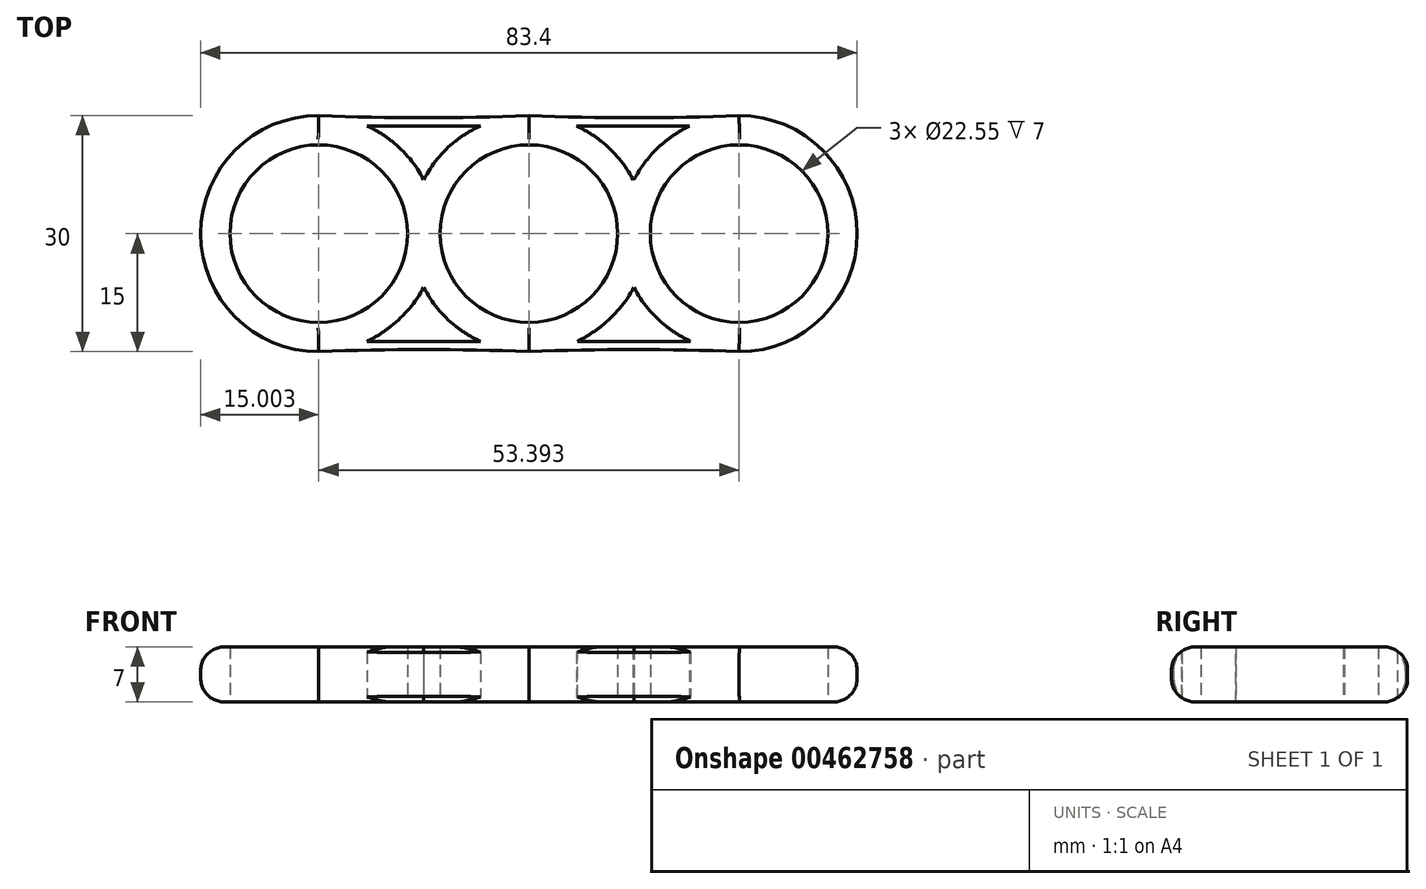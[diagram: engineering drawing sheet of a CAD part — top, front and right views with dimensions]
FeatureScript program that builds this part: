
annotation { "Feature Type Name" : "Feature", "Feature Type Description" : "" }
export const myFeature = defineFeature(function(context is Context, id is Id, definition is map)
    precondition{}
    {
        {
            var Q0;
            Q0=qCreatedBy(makeId("Top.planeOp"),FACE);
            var sketch = newSketch(context, id + "F0", { "sketchPlane" : qUnion([Q0])});
            skCircle(sketch, "E0", {"center": v(0, 0) * mm, "radius": 11.28 * mm});
            skCircle(sketch, "E1", {"center": v(0, 0) * mm, "radius": 15 * mm});
            skCircle(sketch, "E2", {"center": v(0, 0) * mm, "radius": 26.7 * mm});
            skCircle(sketch, "E3", {"center": v(26.7, 0) * mm, "radius": 11.28 * mm});
            skCircle(sketch, "E4", {"center": v(-26.7, 0) * mm, "radius": 11.28 * mm});
            skCircle(sketch, "E5", {"center": v(-26.7, 0) * mm, "radius": 15 * mm});
            skCircle(sketch, "E6", {"center": v(26.7, 0) * mm, "radius": 15 * mm});
            skArc(sketch, "E7", {"start": v(-26.7, 15) * mm, "mid": v(-13.35, 14.72) * mm, "end": v(0, 15) * mm});
            skArc(sketch, "E8", {"start": v(0, 15) * mm, "mid": v(13.35, 14.72) * mm, "end": v(26.7, 15) * mm});
            skArc(sketch, "E9", {"start": v(0, -15) * mm, "mid": v(-13.35, -14.72) * mm, "end": v(-26.7, -15) * mm});
            skArc(sketch, "E10", {"start": v(26.7, -15) * mm, "mid": v(13.35, -14.72) * mm, "end": v(0, -15) * mm});
            skArc(sketch, "E11", {"start": v(-13.35, 6.84) * mm, "mid": v(-16.38, 10.85) * mm, "end": v(-20.54, 13.68) * mm});
            skArc(sketch, "E12", {"start": v(-6.15, 13.68) * mm, "mid": v(-10.28, 10.81) * mm, "end": v(-13.35, 6.84) * mm});
            skLineSegment(sketch, "E13", {"start": v(-20.54, 13.68) * mm, "end": v(-6.15, 13.68) * mm});
            skArc(sketch, "E14", {"start": v(-13.35, -6.84) * mm, "mid": v(-10.31, -10.85) * mm, "end": v(-6.15, -13.68) * mm});
            skArc(sketch, "E15", {"start": v(-20.54, -13.68) * mm, "mid": v(-16.42, -10.81) * mm, "end": v(-13.35, -6.84) * mm});
            skLineSegment(sketch, "E16", {"start": v(-6.15, -13.68) * mm, "end": v(-20.54, -13.68) * mm});
            skArc(sketch, "E17", {"start": v(13.35, -6.84) * mm, "mid": v(16.38, -10.85) * mm, "end": v(20.54, -13.68) * mm});
            skArc(sketch, "E18", {"start": v(6.15, -13.68) * mm, "mid": v(10.28, -10.81) * mm, "end": v(13.35, -6.84) * mm});
            skLineSegment(sketch, "E19", {"start": v(20.54, -13.68) * mm, "end": v(6.15, -13.68) * mm});
            skArc(sketch, "E20", {"start": v(13.23, 6.84) * mm, "mid": v(10.2, 10.85) * mm, "end": v(6.03, 13.68) * mm});
            skArc(sketch, "E21", {"start": v(20.42, 13.68) * mm, "mid": v(16.3, 10.81) * mm, "end": v(13.23, 6.84) * mm});
            skLineSegment(sketch, "E22", {"start": v(6.03, 13.68) * mm, "end": v(20.42, 13.68) * mm});
            skSolve(sketch);
        }
        {
            var Q0;
            {var subQ1=sQuery(id+"F0.wireOp",EDGE,"E5");var subQ3=sQuery(id+"F0.wireOp",EDGE,"E2");var subQ4=makeQuery(id+"F0.imprint","INTERSECT",VERTEX,{"disambiguationData":[OD(0.0)],"derivedFrom":[subQ3,subQ1]});Q0=makeQuery(id+"F0.imprint","IMPRINT",FACE,{"disambiguationData":[TD([[makeQuery(id+"F0.imprint","IMPRINT",EDGE,{"disambiguationData":[TD([[subQ4,-1.0]])],"derivedFrom":subQ3}),-1.0]])]});}
            var Q1;
            {var subQ0=sQuery(id+"F0.wireOp",EDGE,"E5");var subQ1=sQuery(id+"F0.wireOp",EDGE,"E1");var subQ2=makeQuery(id+"F0.imprint","INTERSECT",VERTEX,{"disambiguationData":[OD(0.0)],"derivedFrom":[subQ1,subQ0]});Q1=makeQuery(id+"F0.imprint","IMPRINT",FACE,{"disambiguationData":[TD([[makeQuery(id+"F0.imprint","IMPRINT",EDGE,{"disambiguationData":[TD([[subQ2,-1.0]])],"derivedFrom":subQ1}),1.0]])]});}
            var Q2;
            Q2=makeQuery(id+"F0.imprint","IMPRINT",FACE,{"disambiguationData":[TD([[makeQuery(id+"F0.imprint","IMPRINT",EDGE,{"derivedFrom":sQuery(id+"F0.wireOp",EDGE,"E0")}),-1.0]])]});
            var Q3;
            {var subQ4=sQuery(id+"F0.wireOp",EDGE,"E6");var subQ6=sQuery(id+"F0.wireOp",EDGE,"E1");var subQ7=makeQuery(id+"F0.imprint","INTERSECT",VERTEX,{"disambiguationData":[OD(0.0)],"derivedFrom":[subQ6,subQ4]});Q3=makeQuery(id+"F0.imprint","IMPRINT",FACE,{"disambiguationData":[TD([[makeQuery(id+"F0.imprint","IMPRINT",EDGE,{"disambiguationData":[TD([[subQ7,1.0]])],"derivedFrom":subQ6}),-1.0]])]});}
            var Q4;
            {var subQ0=sQuery(id+"F0.wireOp",EDGE,"E10");var subQ1=sQuery(id+"F0.wireOp",EDGE,"E1");var subQ2=makeQuery(id+"F0.imprint","INTERSECT",VERTEX,{"derivedFrom":[subQ1,subQ0]});Q4=makeQuery(id+"F0.imprint","IMPRINT",FACE,{"disambiguationData":[TD([[makeQuery(id+"F0.imprint","IMPRINT",EDGE,{"disambiguationData":[TD([[subQ2,-1.0]])],"derivedFrom":subQ1}),-1.0]])]});}
            var Q5;
            {var subQ0=sQuery(id+"F0.wireOp",EDGE,"E6");var subQ1=sQuery(id+"F0.wireOp",EDGE,"E1");var subQ2=makeQuery(id+"F0.imprint","INTERSECT",VERTEX,{"disambiguationData":[OD(0.0)],"derivedFrom":[subQ1,subQ0]});Q5=makeQuery(id+"F0.imprint","IMPRINT",FACE,{"disambiguationData":[TD([[makeQuery(id+"F0.imprint","IMPRINT",EDGE,{"disambiguationData":[TD([[subQ2,1.0]])],"derivedFrom":subQ1}),1.0]])]});}
            var Q6;
            {var subQ0=sQuery(id+"F0.wireOp",EDGE,"E7");var subQ1=sQuery(id+"F0.wireOp",EDGE,"E1");var subQ2=makeQuery(id+"F0.imprint","INTERSECT",VERTEX,{"derivedFrom":[subQ1,subQ0]});Q6=makeQuery(id+"F0.imprint","IMPRINT",FACE,{"disambiguationData":[TD([[makeQuery(id+"F0.imprint","IMPRINT",EDGE,{"disambiguationData":[TD([[subQ2,-1.0]])],"derivedFrom":subQ1}),-1.0]])]});}
            var Q7;
            {var subQ0=sQuery(id+"F0.wireOp",EDGE,"E8");var subQ1=sQuery(id+"F0.wireOp",EDGE,"E1");var subQ2=makeQuery(id+"F0.imprint","INTERSECT",VERTEX,{"derivedFrom":[subQ1,subQ0]});Q7=makeQuery(id+"F0.imprint","IMPRINT",FACE,{"disambiguationData":[TD([[makeQuery(id+"F0.imprint","IMPRINT",EDGE,{"disambiguationData":[TD([[subQ2,1.0]])],"derivedFrom":subQ1}),-1.0]])]});}
            var Q8;
            {var subQ1=sQuery(id+"F0.wireOp",EDGE,"E2");var subQ5=sQuery(id+"F0.wireOp",EDGE,"E6");var subQ7=makeQuery(id+"F0.imprint","INTERSECT",VERTEX,{"disambiguationData":[OD(0.0)],"derivedFrom":[subQ1,subQ5]});Q8=makeQuery(id+"F0.imprint","IMPRINT",FACE,{"disambiguationData":[TD([[makeQuery(id+"F0.imprint","IMPRINT",EDGE,{"disambiguationData":[TD([[subQ7,1.0]])],"derivedFrom":subQ1}),-1.0]])]});}
            var Q9;
            {var subQ0=sQuery(id+"F0.wireOp",EDGE,"E7");var subQ1=sQuery(id+"F0.wireOp",EDGE,"E2");var subQ2=makeQuery(id+"F0.imprint","INTERSECT",VERTEX,{"derivedFrom":[subQ1,subQ0]});Q9=makeQuery(id+"F0.imprint","IMPRINT",FACE,{"disambiguationData":[TD([[makeQuery(id+"F0.imprint","IMPRINT",EDGE,{"disambiguationData":[TD([[subQ2,-1.0]])],"derivedFrom":subQ1}),-1.0]])]});}
            var Q10;
            {var subQ0=sQuery(id+"F0.wireOp",EDGE,"E9");var subQ1=sQuery(id+"F0.wireOp",EDGE,"E2");var subQ2=makeQuery(id+"F0.imprint","INTERSECT",VERTEX,{"derivedFrom":[subQ1,subQ0]});Q10=makeQuery(id+"F0.imprint","IMPRINT",FACE,{"disambiguationData":[TD([[makeQuery(id+"F0.imprint","IMPRINT",EDGE,{"disambiguationData":[TD([[subQ2,1.0]])],"derivedFrom":subQ1}),-1.0]])]});}
            var Q11;
            {var subQ0=sQuery(id+"F0.wireOp",EDGE,"E10");var subQ1=sQuery(id+"F0.wireOp",EDGE,"E2");var subQ2=makeQuery(id+"F0.imprint","INTERSECT",VERTEX,{"derivedFrom":[subQ1,subQ0]});Q11=makeQuery(id+"F0.imprint","IMPRINT",FACE,{"disambiguationData":[TD([[makeQuery(id+"F0.imprint","IMPRINT",EDGE,{"disambiguationData":[TD([[subQ2,-1.0]])],"derivedFrom":subQ1}),-1.0]])]});}
            var Q12;
            {var subQ0=sQuery(id+"F0.wireOp",EDGE,"E8");var subQ1=sQuery(id+"F0.wireOp",EDGE,"E2");var subQ2=makeQuery(id+"F0.imprint","INTERSECT",VERTEX,{"derivedFrom":[subQ1,subQ0]});Q12=makeQuery(id+"F0.imprint","IMPRINT",FACE,{"disambiguationData":[TD([[makeQuery(id+"F0.imprint","IMPRINT",EDGE,{"disambiguationData":[TD([[subQ2,1.0]])],"derivedFrom":subQ1}),-1.0]])]});}
            var Q13;
            {var subQ5=sQuery(id+"F0.wireOp",EDGE,"52f5f37f-bad8-4218-8ec9-26ea6716adeb.right");Q13=makeQuery(id+"F0.imprint","IMPRINT",FACE,{"disambiguationData":[TD([[makeQuery(id+"F0.imprint","IMPRINT",EDGE,{"derivedFrom":subQ5}),-1.0]])]});}
            var Q14;
            {var subQ1=sQuery(id+"F0.wireOp",EDGE,"7dec1b2a-d0c0-46ab-8f3a-87d3f4095f80.bottom");Q14=makeQuery(id+"F0.imprint","IMPRINT",FACE,{"disambiguationData":[TD([[makeQuery(id+"F0.imprint","IMPRINT",EDGE,{"derivedFrom":subQ1}),-1.0]])]});}
            var Q15;
            {var subQ5=sQuery(id+"F0.wireOp",EDGE,"9W2gjOTp-DN3G-SVF8-g5jG-bbQzOpd4DBhp.right");Q15=makeQuery(id+"F0.imprint","IMPRINT",FACE,{"disambiguationData":[TD([[makeQuery(id+"F0.imprint","IMPRINT",EDGE,{"derivedFrom":subQ5}),-1.0]])]});}
            var Q16;
            {var subQ5=sQuery(id+"F0.wireOp",EDGE,"f4a26c5c-3129-458d-95a5-6433347c51f9.right");Q16=makeQuery(id+"F0.imprint","IMPRINT",FACE,{"disambiguationData":[TD([[makeQuery(id+"F0.imprint","IMPRINT",EDGE,{"derivedFrom":subQ5}),-1.0]])]});}
            var Q17;
            {var subQ0=sQuery(id+"F0.wireOp",EDGE,"020addc9-02b4-45d7-af9f-7a2b4fcdc8f5.top");Q17=makeQuery(id+"F0.imprint","IMPRINT",FACE,{"disambiguationData":[TD([[makeQuery(id+"F0.imprint","IMPRINT",EDGE,{"derivedFrom":subQ0}),1.0]])]});}
            var Q18;
            {var subQ0=sQuery(id+"F0.wireOp",EDGE,"020addc9-02b4-45d7-af9f-7a2b4fcdc8f5.left");Q18=makeQuery(id+"F0.imprint","IMPRINT",FACE,{"disambiguationData":[TD([[makeQuery(id+"F0.imprint","IMPRINT",EDGE,{"derivedFrom":subQ0}),1.0]])]});}
            var Q19;
            {var subQ5=sQuery(id+"F0.wireOp",EDGE,"f4a26c5c-3129-458d-95a5-6433347c51f9.left");Q19=makeQuery(id+"F0.imprint","IMPRINT",FACE,{"disambiguationData":[TD([[makeQuery(id+"F0.imprint","IMPRINT",EDGE,{"derivedFrom":subQ5}),1.0]])]});}
            var Q20;
            {var subQ5=sQuery(id+"F0.wireOp",EDGE,"9W2gjOTp-DN3G-SVF8-g5jG-bbQzOpd4DBhp.left");Q20=makeQuery(id+"F0.imprint","IMPRINT",FACE,{"disambiguationData":[TD([[makeQuery(id+"F0.imprint","IMPRINT",EDGE,{"derivedFrom":subQ5}),1.0]])]});}
            var Q21;
            {var subQ5=sQuery(id+"F0.wireOp",EDGE,"52f5f37f-bad8-4218-8ec9-26ea6716adeb.left");Q21=makeQuery(id+"F0.imprint","IMPRINT",FACE,{"disambiguationData":[TD([[makeQuery(id+"F0.imprint","IMPRINT",EDGE,{"derivedFrom":subQ5}),1.0]])]});}
            var Q22;
            {var subQ0=sQuery(id+"F0.wireOp",EDGE,"7dec1b2a-d0c0-46ab-8f3a-87d3f4095f80.top");var subQ1=sQuery(id+"F0.wireOp",EDGE,"E6");var subQ2=makeQuery(id+"F0.imprint","INTERSECT",VERTEX,{"derivedFrom":[subQ1,subQ0]});Q22=makeQuery(id+"F0.imprint","IMPRINT",FACE,{"disambiguationData":[TD([[makeQuery(id+"F0.imprint","IMPRINT",EDGE,{"disambiguationData":[TD([[subQ2,-1.0]])],"derivedFrom":subQ1}),1.0]])]});}
            var Q23;
            {var subQ7=sQuery(id+"F0.wireOp",EDGE,"E11");Q23=makeQuery(id+"F0.imprint","IMPRINT",FACE,{"disambiguationData":[TD([[makeQuery(id+"F0.imprint","IMPRINT",EDGE,{"derivedFrom":subQ7}),1.0]])]});}
            var Q24;
            {var subQ0=sQuery(id+"F0.wireOp",EDGE,"E5");var subQ1=sQuery(id+"F0.wireOp",EDGE,"E1");var subQ3=makeQuery(id+"F0.imprint","INTERSECT",VERTEX,{"derivedFrom":[subQ1,subQ0]});Q24=makeQuery(id+"F0.imprint","IMPRINT",FACE,{"disambiguationData":[TD([[makeQuery(id+"F0.imprint","IMPRINT",EDGE,{"disambiguationData":[TD([[subQ3,1.0]])],"derivedFrom":subQ1}),1.0]])]});}
            var Q25;
            {var subQ5=sQuery(id+"F0.wireOp",EDGE,"E16");Q25=makeQuery(id+"F0.imprint","IMPRINT",FACE,{"disambiguationData":[TD([[makeQuery(id+"F0.imprint","IMPRINT",EDGE,{"derivedFrom":subQ5}),1.0]])]});}
            extrude(context, id + "F1", {"entities" : qUnion([Q0, Q1, Q2, Q3, Q4, Q5, Q6, Q7, Q8, Q9, Q10, Q11, Q12, Q13, Q14, Q15, Q16, Q17, Q18, Q19, Q20, Q21, Q22, Q23, Q24, Q25]), "depth" : 7 * mm});
        }
        {
            var Q0;
            Q0=makeQuery(id+"F1.opExtrude","CAP_EDGE",EDGE,{"disambiguationData":[OSD([sQuery(id+"F0.wireOp",EDGE,"E5")])],"isStart":false});
            var Q1;
            Q1=makeQuery(id+"F1.opExtrude","CAP_EDGE",EDGE,{"disambiguationData":[OSD([sQuery(id+"F0.wireOp",EDGE,"E9")])],"isStart":false});
            var Q2;
            Q2=makeQuery(id+"F1.opExtrude","CAP_EDGE",EDGE,{"disambiguationData":[OSD([sQuery(id+"F0.wireOp",EDGE,"E10")])],"isStart":false});
            var Q3;
            Q3=makeQuery(id+"F1.opExtrude","CAP_EDGE",EDGE,{"disambiguationData":[OSD([sQuery(id+"F0.wireOp",EDGE,"E7")])],"isStart":false});
            var Q4;
            Q4=makeQuery(id+"F1.opExtrude","CAP_EDGE",EDGE,{"disambiguationData":[OSD([sQuery(id+"F0.wireOp",EDGE,"E8")])],"isStart":false});
            var Q5;
            {var subQ0=sQuery(id+"F0.wireOp",EDGE,"E6");Q5=makeQuery(id+"F1.opExtrude","CAP_EDGE",EDGE,{"disambiguationData":[OSD([subQ0]),TDD([makeQuery(id+"F0.imprint","IMPRINT",EDGE,{"disambiguationData":[TD([[makeQuery(id+"F0.imprint","INTERSECT",VERTEX,{"disambiguationData":[OD(0.0)],"derivedFrom":[subQ0,sQuery(id+"F0.wireOp",EDGE,"E8")]}),1.0]])],"derivedFrom":subQ0})])],"isStart":false});}
            fillet(context, id + "F2", {"entities" : qUnion([Q0, Q1, Q2, Q3, Q4, Q5]), "radius" : 3 * mm, "tangentPropagation" : true, "allowEdgeOverflow" : false});
        }
        {
            var Q0;
            Q0=makeQuery(id+"F1.opExtrude","CAP_EDGE",EDGE,{"disambiguationData":[OSD([sQuery(id+"F0.wireOp",EDGE,"E9")])],"isStart":true});
            var Q1;
            Q1=makeQuery(id+"F1.opExtrude","CAP_EDGE",EDGE,{"disambiguationData":[OSD([sQuery(id+"F0.wireOp",EDGE,"E5")])],"isStart":true});
            var Q2;
            Q2=makeQuery(id+"F1.opExtrude","CAP_EDGE",EDGE,{"disambiguationData":[OSD([sQuery(id+"F0.wireOp",EDGE,"E7")])],"isStart":true});
            var Q3;
            Q3=makeQuery(id+"F1.opExtrude","CAP_EDGE",EDGE,{"disambiguationData":[OSD([sQuery(id+"F0.wireOp",EDGE,"E8")])],"isStart":true});
            var Q4;
            Q4=makeQuery(id+"F1.opExtrude","CAP_EDGE",EDGE,{"disambiguationData":[OSD([sQuery(id+"F0.wireOp",EDGE,"E10")])],"isStart":true});
            var Q5;
            {var subQ0=sQuery(id+"F0.wireOp",EDGE,"E6");Q5=makeQuery(id+"F1.opExtrude","CAP_EDGE",EDGE,{"disambiguationData":[OSD([subQ0]),TDD([makeQuery(id+"F0.imprint","IMPRINT",EDGE,{"disambiguationData":[TD([[makeQuery(id+"F0.imprint","INTERSECT",VERTEX,{"disambiguationData":[OD(0.0)],"derivedFrom":[subQ0,sQuery(id+"F0.wireOp",EDGE,"E8")]}),1.0]])],"derivedFrom":subQ0})])],"isStart":true});}
            fillet(context, id + "F3", {"entities" : qUnion([Q0, Q1, Q2, Q3, Q4, Q5]), "radius" : 3 * mm, "tangentPropagation" : true, "allowEdgeOverflow" : false});
        }
    });
